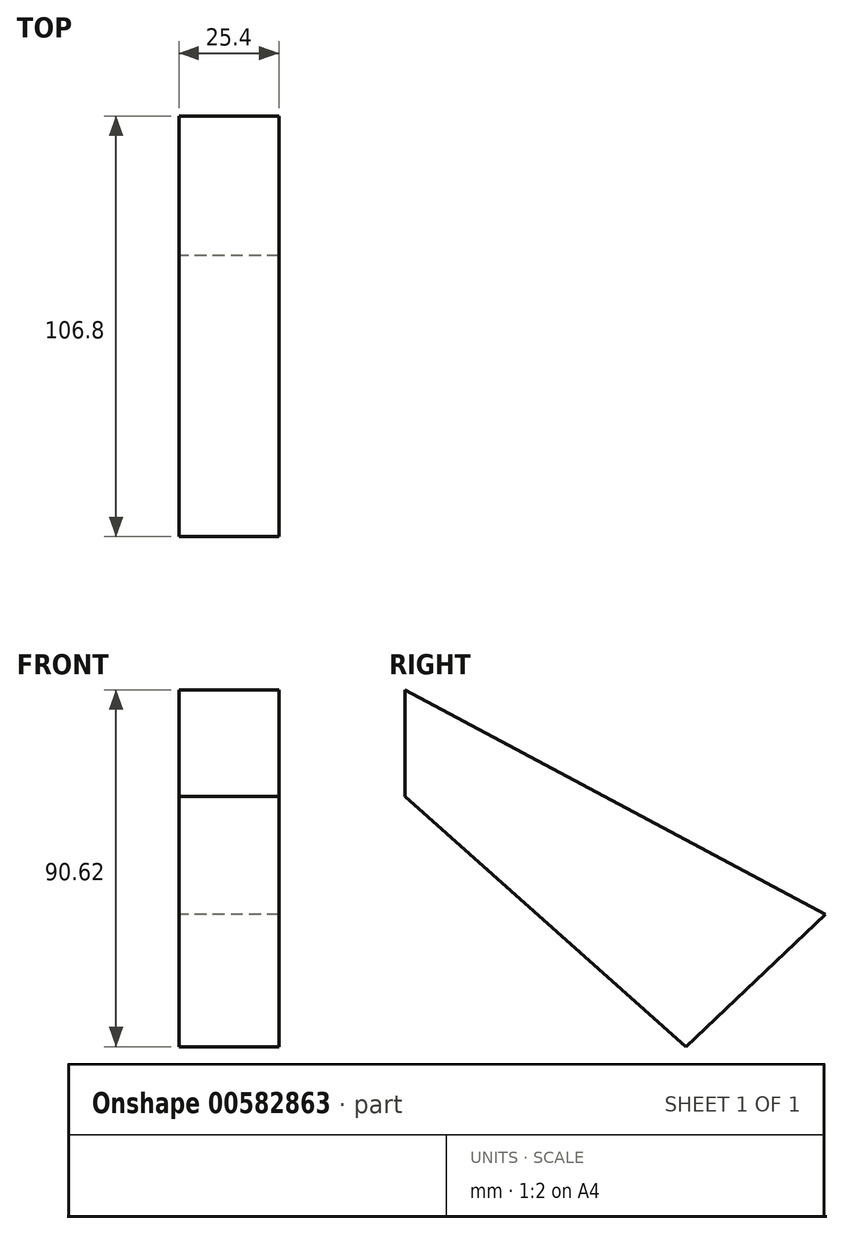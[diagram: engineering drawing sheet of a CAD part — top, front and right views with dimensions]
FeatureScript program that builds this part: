
annotation { "Feature Type Name" : "Feature", "Feature Type Description" : "" }
export const myFeature = defineFeature(function(context is Context, id is Id, definition is map)
    precondition{}
    {
        {
            var Q0;
            Q0=qCreatedBy(makeId("Right.planeOp"),FACE);
            var sketch = newSketch(context, id + "F0", { "sketchPlane" : qUnion([Q0])});
            skLineSegment(sketch, "E0", {"start": v(-94.52, 90.62) * mm, "end": v(12.28, 33.6) * mm});
            skLineSegment(sketch, "E1", {"start": v(12.28, 33.6) * mm, "end": v(-23.13, 0) * mm});
            skLineSegment(sketch, "E2", {"start": v(-23.13, 0) * mm, "end": v(-94.52, 63.58) * mm});
            skLineSegment(sketch, "E3", {"start": v(-94.52, 63.58) * mm, "end": v(-94.52, 90.62) * mm});
            skSolve(sketch);
        }
        {
            var Q0;
            Q0=makeQuery(id+"F0.imprint","IMPRINT",FACE,{"disambiguationData":[TD([[makeQuery(id+"F0.imprint","IMPRINT",EDGE,{"derivedFrom":sQuery(id+"F0.wireOp",EDGE,"E0")}),-1.0]])]});
            extrude(context, id + "F1", {"entities" : qUnion([Q0]), "depth" : 25.4 * mm, "offsetDistance" : 25.4 * mm});
        }
    });
